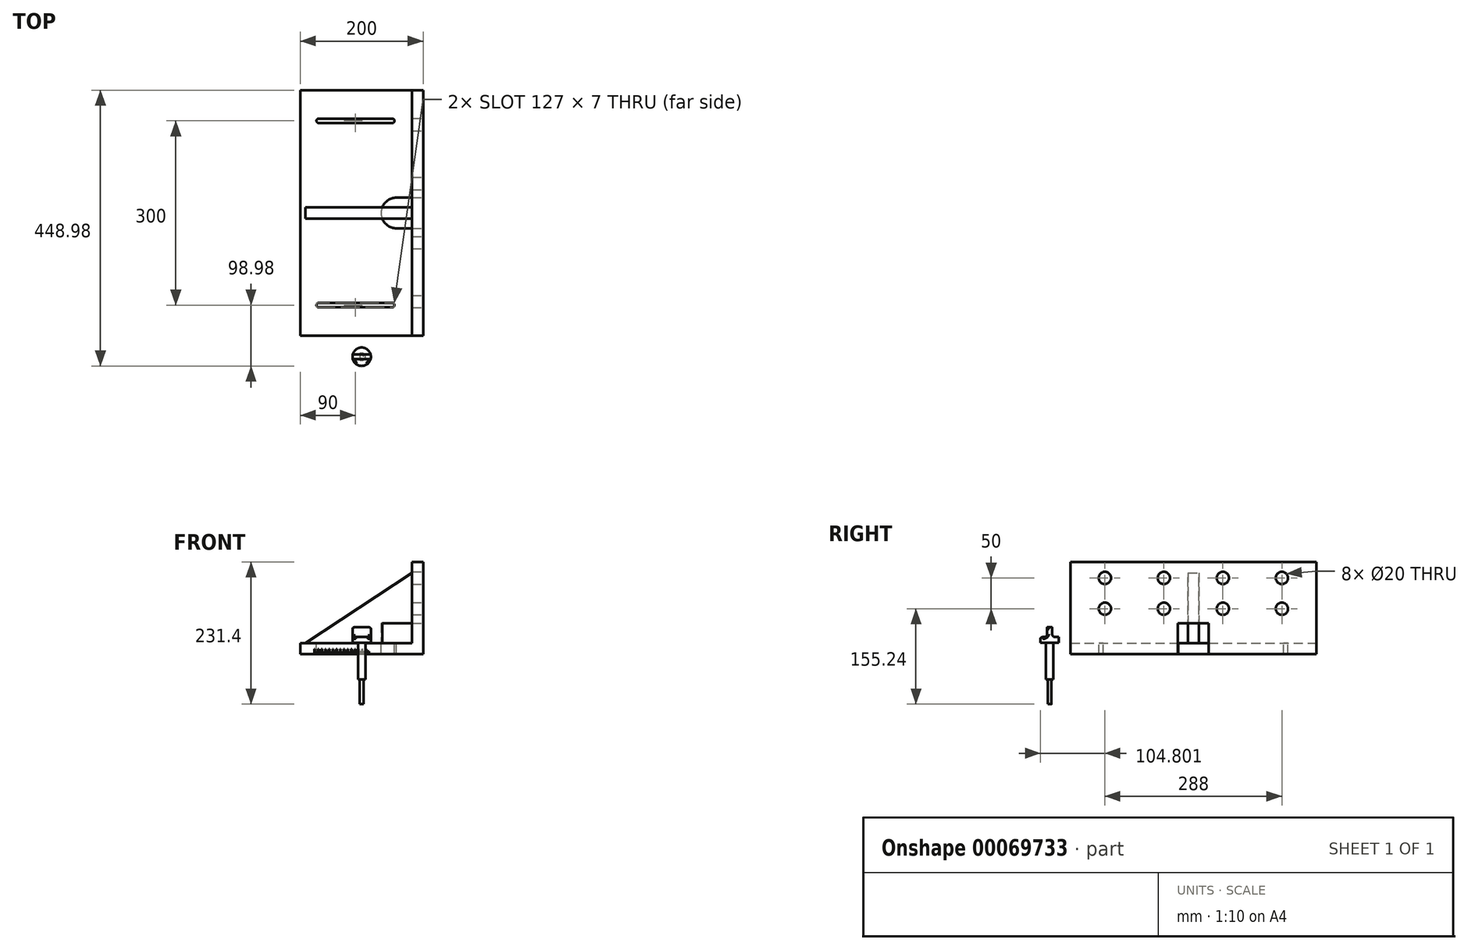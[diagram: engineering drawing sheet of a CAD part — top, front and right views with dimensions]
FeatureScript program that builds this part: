
annotation { "Feature Type Name" : "Feature", "Feature Type Description" : "" }
export const myFeature = defineFeature(function(context is Context, id is Id, definition is map)
    precondition{}
    {
        {
            var Q0;
            Q0=qCreatedBy(makeId("Front.planeOp"),FACE);
            var sketch = newSketch(context, id + "F0", { "sketchPlane" : qUnion([Q0])});
            skLineSegment(sketch, "E0.bottom", {"start": v(-100, -37.42) * mm, "end": v(82, -37.42) * mm});
            skLineSegment(sketch, "E0.top", {"start": v(-100, -55.42) * mm, "end": v(100, -55.42) * mm});
            skLineSegment(sketch, "E0.left", {"start": v(-100, -37.42) * mm, "end": v(-100, -55.42) * mm});
            skLineSegment(sketch, "E0.right", {"start": v(100, -37.42) * mm, "end": v(100, -55.42) * mm});
            skLineSegment(sketch, "E1", {"start": v(100, -37.42) * mm, "end": v(100, 94.58) * mm});
            skLineSegment(sketch, "E2", {"start": v(100, 94.58) * mm, "end": v(82, 94.58) * mm});
            skLineSegment(sketch, "E3", {"start": v(82, 94.58) * mm, "end": v(82, -37.42) * mm});
            skLineSegment(sketch, "E4", {"start": v(-91.58, -37.42) * mm, "end": v(82, 76.61) * mm});
            skSolve(sketch);
        }
        {
            var Q0;
            Q0=makeQuery(id+"F0.imprint","IMPRINT",FACE,{"disambiguationData":[TD([[makeQuery(id+"F0.imprint","IMPRINT",EDGE,{"derivedFrom":sQuery(id+"F0.wireOp",EDGE,"E0.bottom")}),-1.0]])]});
            extrude(context, id + "F1", {"entities" : qUnion([Q0]), "endBound" : BoundingType.SYMMETRIC, "depth" : 400 * mm});
        }
        {
            var Q0;
            Q0=makeQuery(id+"F1.opExtrude","SWEPT_FACE",FACE,{"disambiguationData":[OSD([sQuery(id+"F0.wireOp",EDGE,"E0.bottom")])]});
            var sketch = newSketch(context, id + "F2", { "sketchPlane" : qUnion([Q0])});
            skArc(sketch, "E5", {"start": v(-70, 153.5) * mm, "mid": v(-73.5, 150) * mm, "end": v(-70, 146.5) * mm});
            skArc(sketch, "E6", {"start": v(50, 146.5) * mm, "mid": v(53.5, 150) * mm, "end": v(50, 153.5) * mm});
            skLineSegment(sketch, "E7", {"start": v(-70, 153.5) * mm, "end": v(50, 153.5) * mm});
            skLineSegment(sketch, "E8", {"start": v(-70, 146.5) * mm, "end": v(50, 146.5) * mm});
            skLineSegment(sketch, "E9", {"start": v(-70, -153.5) * mm, "end": v(50, -153.5) * mm});
            skLineSegment(sketch, "E10", {"start": v(-70, -146.5) * mm, "end": v(50, -146.5) * mm});
            skArc(sketch, "E11", {"start": v(50, -153.5) * mm, "mid": v(53.5, -150) * mm, "end": v(50, -146.5) * mm});
            skArc(sketch, "E12", {"start": v(-70, -146.5) * mm, "mid": v(-73.5, -150) * mm, "end": v(-70, -153.5) * mm});
            skArc(sketch, "E13", {"start": v(56.66, 25) * mm, "mid": v(31.66, 0) * mm, "end": v(56.66, -25) * mm});
            skLineSegment(sketch, "E14.bottom", {"start": v(56.66, 25) * mm, "end": v(82, 25) * mm});
            skLineSegment(sketch, "E14.top", {"start": v(56.66, -25.18) * mm, "end": v(82, -25.18) * mm});
            skLineSegment(sketch, "E14.right", {"start": v(82, 25) * mm, "end": v(82, -25.18) * mm});
            skLineSegment(sketch, "E15.trimOffspring", {"start": v(56.66, -25) * mm, "end": v(56.66, -25.18) * mm});
            skSolve(sketch);
        }
        {
            var Q0;
            Q0=makeQuery(id+"F2.imprint","IMPRINT",FACE,{"disambiguationData":[TD([[makeQuery(id+"F2.imprint","IMPRINT",EDGE,{"derivedFrom":sQuery(id+"F2.wireOp",EDGE,"E5")}),1.0]])]});
            var Q1;
            Q1=makeQuery(id+"F2.imprint","IMPRINT",FACE,{"disambiguationData":[TD([[makeQuery(id+"F2.imprint","IMPRINT",EDGE,{"derivedFrom":sQuery(id+"F2.wireOp",EDGE,"E9")}),1.0]])]});
            var Q2;
            Q2=makeQuery(id+"F2.imprint","IMPRINT",FACE,{"disambiguationData":[TD([[makeQuery(id+"F2.imprint","IMPRINT",EDGE,{"derivedFrom":sQuery(id+"F2.wireOp",EDGE,"E13")}),1.0]])]});
            extrude(context, id + "F3", {"entities" : qUnion([Q0, Q1, Q2]), "operationType" : NewBodyOperationType.REMOVE, "oppositeDirection" : true, "depth" : 22 * mm});
        }
        {
            var Q0;
            Q0=makeQuery(id+"F1.opExtrude","SWEPT_FACE",FACE,{"disambiguationData":[OSD([sQuery(id+"F0.wireOp",EDGE,"E0.right"),sQuery(id+"F0.wireOp",EDGE,"E1")])]});
            var sketch = newSketch(context, id + "F4", { "sketchPlane" : qUnion([Q0])});
            skLineSegment(sketch, "E16.0", {"start": v(-25.18, -55.42) * mm, "end": v(-25.18, -37.42) * mm});
            skLineSegment(sketch, "E16.1", {"start": v(25, -55.42) * mm, "end": v(25, -37.42) * mm});
            skLineSegment(sketch, "E17.bottom", {"start": v(-25.18, -55.42) * mm, "end": v(25, -55.42) * mm});
            skLineSegment(sketch, "E17.top", {"start": v(-25.18, -5.42) * mm, "end": v(25, -5.42) * mm});
            skLineSegment(sketch, "E17.left", {"start": v(-25.18, -55.42) * mm, "end": v(-25.18, -5.42) * mm});
            skLineSegment(sketch, "E17.right", {"start": v(25, -55.42) * mm, "end": v(25, -5.42) * mm});
            skCircle(sketch, "E18", {"center": v(-144.18, 68.42) * mm, "radius": 10 * mm});
            skCircle(sketch, "E19.0.1.0", {"center": v(-144.18, 18.42) * mm, "radius": 10 * mm});
            skCircle(sketch, "E19.1.0.0", {"center": v(-48.18, 68.42) * mm, "radius": 10 * mm});
            skCircle(sketch, "E19.1.1.0", {"center": v(-48.18, 18.42) * mm, "radius": 10 * mm});
            skCircle(sketch, "E19.2.0.0", {"center": v(47.82, 68.42) * mm, "radius": 10 * mm});
            skCircle(sketch, "E19.2.1.0", {"center": v(47.82, 18.42) * mm, "radius": 10 * mm});
            skCircle(sketch, "E19.3.0.0", {"center": v(143.82, 68.42) * mm, "radius": 10 * mm});
            skCircle(sketch, "E19.3.1.0", {"center": v(143.82, 18.42) * mm, "radius": 10 * mm});
            skLineSegment(sketch, "E19.direction1", {"start": v(-144.18, 68.42) * mm, "end": v(-48.18, 68.42) * mm, "construction": true});
            skLineSegment(sketch, "E19.direction2", {"start": v(-144.18, 68.42) * mm, "end": v(-144.18, 18.42) * mm, "construction": true});
            skSolve(sketch);
        }
        {
            var Q0;
            Q0=makeQuery(id+"F4.imprint","IMPRINT",FACE,{"disambiguationData":[TD([[makeQuery(id+"F4.imprint","IMPRINT",EDGE,{"derivedFrom":sQuery(id+"F4.wireOp",EDGE,"E18")}),1.0]])]});
            var Q1;
            Q1=makeQuery(id+"F4.imprint","IMPRINT",FACE,{"disambiguationData":[TD([[makeQuery(id+"F4.imprint","IMPRINT",EDGE,{"derivedFrom":sQuery(id+"F4.wireOp",EDGE,"E19.0.1.0")}),1.0]])]});
            var Q2;
            Q2=makeQuery(id+"F4.imprint","IMPRINT",FACE,{"disambiguationData":[TD([[makeQuery(id+"F4.imprint","IMPRINT",EDGE,{"derivedFrom":sQuery(id+"F4.wireOp",EDGE,"E19.1.1.0")}),1.0]])]});
            var Q3;
            Q3=makeQuery(id+"F4.imprint","IMPRINT",FACE,{"disambiguationData":[TD([[makeQuery(id+"F4.imprint","IMPRINT",EDGE,{"derivedFrom":sQuery(id+"F4.wireOp",EDGE,"E19.1.0.0")}),1.0]])]});
            var Q4;
            Q4=makeQuery(id+"F4.imprint","IMPRINT",FACE,{"disambiguationData":[TD([[makeQuery(id+"F4.imprint","IMPRINT",EDGE,{"derivedFrom":sQuery(id+"F4.wireOp",EDGE,"E19.2.0.0")}),1.0]])]});
            var Q5;
            Q5=makeQuery(id+"F4.imprint","IMPRINT",FACE,{"disambiguationData":[TD([[makeQuery(id+"F4.imprint","IMPRINT",EDGE,{"derivedFrom":sQuery(id+"F4.wireOp",EDGE,"E19.2.1.0")}),1.0]])]});
            var Q6;
            Q6=makeQuery(id+"F4.imprint","IMPRINT",FACE,{"disambiguationData":[TD([[makeQuery(id+"F4.imprint","IMPRINT",EDGE,{"derivedFrom":sQuery(id+"F4.wireOp",EDGE,"E19.3.1.0")}),1.0]])]});
            var Q7;
            Q7=makeQuery(id+"F4.imprint","IMPRINT",FACE,{"disambiguationData":[TD([[makeQuery(id+"F4.imprint","IMPRINT",EDGE,{"derivedFrom":sQuery(id+"F4.wireOp",EDGE,"E19.3.0.0")}),1.0]])]});
            var Q8;
            {var subQ7=sQuery(id+"F4.wireOp",EDGE,"E17.top");Q8=makeQuery(id+"F4.imprint","IMPRINT",FACE,{"disambiguationData":[TD([[makeQuery(id+"F4.imprint","IMPRINT",EDGE,{"derivedFrom":subQ7}),-1.0]])]});}
            extrude(context, id + "F5", {"entities" : qUnion([Q0, Q1, Q2, Q3, Q4, Q5, Q6, Q7, Q8]), "operationType" : NewBodyOperationType.REMOVE, "oppositeDirection" : true, "depth" : 25 * mm});
        }
        {
            var Q0;
            {var subQ3=sQuery(id+"F0.wireOp",EDGE,"E4");Q0=makeQuery(id+"F0.imprint","IMPRINT",FACE,{"disambiguationData":[TD([[makeQuery(id+"F0.imprint","IMPRINT",EDGE,{"derivedFrom":subQ3}),-1.0]])]});}
            extrude(context, id + "F6", {"entities" : qUnion([Q0]), "endBound" : BoundingType.SYMMETRIC, "depth" : 18 * mm});
        }
        {
            var Q0;
            Q0=makeQuery(id+"F2.imprint","IMPRINT",FACE,{"disambiguationData":[TD([[makeQuery(id+"F2.imprint","IMPRINT",EDGE,{"derivedFrom":sQuery(id+"F2.wireOp",EDGE,"E13")}),1.0]])]});
            extrude(context, id + "F7", {"entities" : qUnion([Q0]), "operationType" : NewBodyOperationType.REMOVE, "depth" : 32 * mm});
        }
        {
            var Q0;
            Q0=qCreatedBy(makeId("Right.planeOp"),FACE);
            var sketch = newSketch(context, id + "F8", { "sketchPlane" : qUnion([Q0])});
            skLineSegment(sketch, "E20", {"start": v(-233.98, 65.01) * mm, "end": v(-233.98, -136.22) * mm, "construction": true});
            skLineSegment(sketch, "E21", {"start": v(-233.98, -136.82) * mm, "end": v(-236.98, -136.82) * mm});
            skLineSegment(sketch, "E22", {"start": v(-236.98, -136.82) * mm, "end": v(-236.98, -96.82) * mm});
            skLineSegment(sketch, "E23", {"start": v(-236.98, -96.82) * mm, "end": v(-239.98, -96.82) * mm});
            skLineSegment(sketch, "E24", {"start": v(-239.98, -96.82) * mm, "end": v(-239.98, -36.82) * mm});
            skLineSegment(sketch, "E25", {"start": v(-239.98, -36.82) * mm, "end": v(-248.98, -36.82) * mm});
            skLineSegment(sketch, "E26", {"start": v(-248.98, -36.82) * mm, "end": v(-248.98, -11.82) * mm});
            skLineSegment(sketch, "E27", {"start": v(-248.98, -11.82) * mm, "end": v(-233.98, -11.82) * mm});
            skLineSegment(sketch, "E28", {"start": v(-233.98, -136.82) * mm, "end": v(-233.98, -11.82) * mm});
            skSolve(sketch);
        }
        {
            var Q0;
            Q0=makeQuery(id+"F8.imprint","IMPRINT",FACE,{"disambiguationData":[TD([[makeQuery(id+"F8.imprint","IMPRINT",EDGE,{"derivedFrom":sQuery(id+"F8.wireOp",EDGE,"E21")}),-1.0]])]});
            var Q1;
            Q1=sQuery(id+"F8.wireOp",EDGE,"E20");
            revolve(context, id + "F9", {"entities" : qUnion([Q0]), "axis" : qUnion([Q1]), "revolveType" : RevolveType.FULL});
        }
        {
            var Q0;
            Q0=makeQuery(id+"F9.opRevolve","SWEPT_FACE",FACE,{"disambiguationData":[OSD([sQuery(id+"F8.wireOp",EDGE,"E27")])]});
            var sketch = newSketch(context, id + "F10", { "sketchPlane" : qUnion([Q0])});
            skLineSegment(sketch, "E29.bottom", {"start": v(17.05, -237.98) * mm, "end": v(-19.1, -237.98) * mm});
            skLineSegment(sketch, "E29.top", {"start": v(17.05, -250.11) * mm, "end": v(-19.1, -250.11) * mm});
            skLineSegment(sketch, "E29.left", {"start": v(17.05, -237.98) * mm, "end": v(17.05, -250.11) * mm});
            skLineSegment(sketch, "E29.right", {"start": v(-19.1, -237.98) * mm, "end": v(-19.1, -250.11) * mm});
            skLineSegment(sketch, "E30.bottom", {"start": v(17.68, -229.98) * mm, "end": v(-19.15, -229.98) * mm});
            skLineSegment(sketch, "E30.top", {"start": v(17.68, -217.98) * mm, "end": v(-19.15, -217.98) * mm});
            skLineSegment(sketch, "E30.left", {"start": v(17.68, -229.98) * mm, "end": v(17.68, -217.98) * mm});
            skLineSegment(sketch, "E30.right", {"start": v(-19.15, -229.98) * mm, "end": v(-19.15, -217.98) * mm});
            skSolve(sketch);
        }
        {
            var Q0;
            {var subQ0=sQuery(id+"F10.wireOp",EDGE,"E29.bottom");var subQ1=makeQuery(id+"F9.opRevolve","SWEPT_EDGE",EDGE,{"disambiguationData":[OSD([sQuery(id+"F8.wireOp",EDGE,"E26"),sQuery(id+"F8.wireOp",EDGE,"E27")])]});var subQ2=makeQuery(id+"F10.imprint","INTERSECT",VERTEX,{"disambiguationData":[OD(0.0)],"derivedFrom":[subQ1,subQ0]});Q0=makeQuery(id+"F10.imprint","IMPRINT",FACE,{"disambiguationData":[TD([[makeQuery(id+"F10.imprint","IMPRINT",EDGE,{"disambiguationData":[TD([[subQ2,-1.0]])],"derivedFrom":subQ0}),1.0]])]});}
            var Q1;
            Q1=makeQuery(id+"F10.imprint","IMPRINT",FACE,{"disambiguationData":[TD([[makeQuery(id+"F10.imprint","IMPRINT",EDGE,{"derivedFrom":sQuery(id+"F10.wireOp",EDGE,"E29.top")}),-1.0]])]});
            var Q2;
            {var subQ0=sQuery(id+"F10.wireOp",EDGE,"E30.bottom");var subQ1=makeQuery(id+"F9.opRevolve","SWEPT_EDGE",EDGE,{"disambiguationData":[OSD([sQuery(id+"F8.wireOp",EDGE,"E26"),sQuery(id+"F8.wireOp",EDGE,"E27")])]});var subQ2=makeQuery(id+"F10.imprint","INTERSECT",VERTEX,{"disambiguationData":[OD(0.0)],"derivedFrom":[subQ1,subQ0]});Q2=makeQuery(id+"F10.imprint","IMPRINT",FACE,{"disambiguationData":[TD([[makeQuery(id+"F10.imprint","IMPRINT",EDGE,{"disambiguationData":[TD([[subQ2,-1.0]])],"derivedFrom":subQ0}),-1.0]])]});}
            extrude(context, id + "F11", {"entities" : qUnion([Q0, Q1, Q2]), "operationType" : NewBodyOperationType.REMOVE, "oppositeDirection" : true, "depth" : 16 * mm});
        }
        {
            var Q0;
            Q0=makeQuery(id+"F11.boolean.opBoolean","COPY",EDGE,{"derivedFrom":makeQuery(id+"F11.opExtrude","CAP_EDGE",EDGE,{"disambiguationData":[OSD([sQuery(id+"F10.wireOp",EDGE,"E29.bottom")])],"isStart":false})});
            var Q1;
            Q1=makeQuery(id+"F11.boolean.opBoolean","COPY",EDGE,{"derivedFrom":makeQuery(id+"F11.opExtrude","CAP_EDGE",EDGE,{"disambiguationData":[OSD([sQuery(id+"F10.wireOp",EDGE,"E30.bottom")])],"isStart":false})});
            fillet(context, id + "F12", {"entities" : qUnion([Q0, Q1]), "radius" : 5 * mm, "tangentPropagation" : true, "allowEdgeOverflow" : false});
        }
        {
            var Q0;
            Q0=makeQuery(id+"F11.boolean.opBoolean","INTERSECT",EDGE,{"disambiguationData":[OD(0.0)],"derivedFrom":[makeQuery(id+"F9.opRevolve","SWEPT_FACE",FACE,{"disambiguationData":[OSD([sQuery(id+"F8.wireOp",EDGE,"E26")])]}),makeQuery(id+"F11.opExtrude","SWEPT_FACE",FACE,{"disambiguationData":[OSD([sQuery(id+"F10.wireOp",EDGE,"E29.bottom")])]})]});
            var Q1;
            {var subQ0=sQuery(id+"F10.wireOp",EDGE,"E30.bottom");var subQ1=sQuery(id+"F8.wireOp",EDGE,"E27");var subQ2=sQuery(id+"F8.wireOp",EDGE,"E26");Q1=makeQuery(id+"F11.boolean.opBoolean","COPY",EDGE,{"derivedFrom":makeQuery(id+"F11.opExtrude","SWEPT_EDGE",EDGE,{"disambiguationData":[OSD([subQ2,subQ1,subQ0]),TDD([makeQuery(id+"F10.imprint","INTERSECT",VERTEX,{"disambiguationData":[OD(0.0)],"derivedFrom":[makeQuery(id+"F9.opRevolve","SWEPT_EDGE",EDGE,{"disambiguationData":[OSD([subQ2,subQ1])]}),subQ0]})])]})});}
            var Q2;
            Q2=makeQuery(id+"F11.boolean.opBoolean","SPLIT",EDGE,{"disambiguationData":[OD(0.0)],"derivedFrom":makeQuery(id+"F9.opRevolve","SWEPT_EDGE",EDGE,{"disambiguationData":[OSD([sQuery(id+"F8.wireOp",EDGE,"E26"),sQuery(id+"F8.wireOp",EDGE,"E27")])]})});
            var Q3;
            Q3=makeQuery(id+"F11.boolean.opBoolean","COPY",EDGE,{"derivedFrom":makeQuery(id+"F11.opExtrude","CAP_EDGE",EDGE,{"disambiguationData":[OSD([sQuery(id+"F10.wireOp",EDGE,"E29.bottom")])],"isStart":true})});
            var Q4;
            Q4=makeQuery(id+"F11.boolean.opBoolean","COPY",EDGE,{"derivedFrom":makeQuery(id+"F11.opExtrude","CAP_EDGE",EDGE,{"disambiguationData":[OSD([sQuery(id+"F10.wireOp",EDGE,"E30.bottom")])],"isStart":true})});
            var Q5;
            Q5=makeQuery(id+"F11.boolean.opBoolean","INTERSECT",EDGE,{"disambiguationData":[OD(1.0)],"derivedFrom":[makeQuery(id+"F9.opRevolve","SWEPT_FACE",FACE,{"disambiguationData":[OSD([sQuery(id+"F8.wireOp",EDGE,"E26")])]}),makeQuery(id+"F11.opExtrude","SWEPT_FACE",FACE,{"disambiguationData":[OSD([sQuery(id+"F10.wireOp",EDGE,"E29.bottom")])]})]});
            var Q6;
            {var subQ0=sQuery(id+"F10.wireOp",EDGE,"E30.bottom");var subQ1=sQuery(id+"F8.wireOp",EDGE,"E27");var subQ2=sQuery(id+"F8.wireOp",EDGE,"E26");Q6=makeQuery(id+"F11.boolean.opBoolean","COPY",EDGE,{"derivedFrom":makeQuery(id+"F11.opExtrude","SWEPT_EDGE",EDGE,{"disambiguationData":[OSD([subQ2,subQ1,subQ0]),TDD([makeQuery(id+"F10.imprint","INTERSECT",VERTEX,{"disambiguationData":[OD(1.0)],"derivedFrom":[makeQuery(id+"F9.opRevolve","SWEPT_EDGE",EDGE,{"disambiguationData":[OSD([subQ2,subQ1])]}),subQ0]})])]})});}
            var Q7;
            Q7=makeQuery(id+"F11.boolean.opBoolean","SPLIT",EDGE,{"disambiguationData":[OD(1.0)],"derivedFrom":makeQuery(id+"F9.opRevolve","SWEPT_EDGE",EDGE,{"disambiguationData":[OSD([sQuery(id+"F8.wireOp",EDGE,"E26"),sQuery(id+"F8.wireOp",EDGE,"E27")])]})});
            fillet(context, id + "F13", {"entities" : qUnion([Q0, Q1, Q2, Q3, Q4, Q5, Q6, Q7]), "radius" : 3 * mm, "tangentPropagation" : true, "allowEdgeOverflow" : false});
        }
        {
            var Q0;
            Q0=makeQuery(id+"F1.opExtrude","CAP_FACE",FACE,{"disambiguationData":[OSD([sQuery(id+"F0.wireOp",EDGE,"E0.bottom"),sQuery(id+"F0.wireOp",EDGE,"E0.top"),sQuery(id+"F0.wireOp",EDGE,"E0.left"),sQuery(id+"F0.wireOp",EDGE,"E0.right"),sQuery(id+"F0.wireOp",EDGE,"E1"),sQuery(id+"F0.wireOp",EDGE,"E2"),sQuery(id+"F0.wireOp",EDGE,"E3")])],"isStart":false});
            var sketch = newSketch(context, id + "F14", { "sketchPlane" : qUnion([Q0])});
            skLineSegment(sketch, "E31.bottom", {"start": v(-77.2, -55.42) * mm, "end": v(-76.2, -55.42) * mm});
            skLineSegment(sketch, "E31.top", {"start": v(-77.2, -47.42) * mm, "end": v(-76.2, -47.42) * mm});
            skLineSegment(sketch, "E31.left", {"start": v(-77.2, -55.42) * mm, "end": v(-77.2, -47.42) * mm});
            skLineSegment(sketch, "E31.right", {"start": v(-76.2, -55.42) * mm, "end": v(-76.2, -47.42) * mm});
            skLineSegment(sketch, "E32.bottom", {"start": v(-75.2, -55.42) * mm, "end": v(-74.2, -55.42) * mm});
            skLineSegment(sketch, "E32.top", {"start": v(-75.2, -50.86) * mm, "end": v(-74.2, -50.86) * mm});
            skLineSegment(sketch, "E32.left", {"start": v(-75.2, -55.42) * mm, "end": v(-75.2, -50.86) * mm});
            skLineSegment(sketch, "E32.right", {"start": v(-74.2, -55.42) * mm, "end": v(-74.2, -50.86) * mm});
            skLineSegment(sketch, "E33.bottom", {"start": v(-73.2, -55.42) * mm, "end": v(-72.2, -55.42) * mm});
            skLineSegment(sketch, "E33.top", {"start": v(-73.2, -50.86) * mm, "end": v(-72.2, -50.86) * mm});
            skLineSegment(sketch, "E33.left", {"start": v(-73.2, -55.42) * mm, "end": v(-73.2, -50.86) * mm});
            skLineSegment(sketch, "E33.right", {"start": v(-72.2, -55.42) * mm, "end": v(-72.2, -50.86) * mm});
            skLineSegment(sketch, "E34.1.0.0", {"start": v(-69.2, -55.42) * mm, "end": v(-69.2, -50.86) * mm});
            skLineSegment(sketch, "E34.1.0.1", {"start": v(-70.2, -55.42) * mm, "end": v(-70.2, -47.42) * mm});
            skLineSegment(sketch, "E34.1.0.2", {"start": v(-71.2, -55.42) * mm, "end": v(-71.2, -47.42) * mm});
            skLineSegment(sketch, "E34.1.0.3", {"start": v(-68.2, -55.42) * mm, "end": v(-68.2, -50.86) * mm});
            skLineSegment(sketch, "E34.1.0.4", {"start": v(-67.2, -55.42) * mm, "end": v(-66.2, -55.42) * mm});
            skLineSegment(sketch, "E34.1.0.5", {"start": v(-67.2, -50.86) * mm, "end": v(-66.2, -50.86) * mm});
            skLineSegment(sketch, "E34.1.0.6", {"start": v(-67.2, -55.42) * mm, "end": v(-67.2, -50.86) * mm});
            skLineSegment(sketch, "E34.1.0.7", {"start": v(-66.2, -55.42) * mm, "end": v(-66.2, -50.86) * mm});
            skLineSegment(sketch, "E34.1.0.8", {"start": v(-69.2, -50.86) * mm, "end": v(-68.2, -50.86) * mm});
            skLineSegment(sketch, "E34.1.0.9", {"start": v(-69.2, -55.42) * mm, "end": v(-68.2, -55.42) * mm});
            skLineSegment(sketch, "E34.1.0.10", {"start": v(-71.2, -47.42) * mm, "end": v(-70.2, -47.42) * mm});
            skLineSegment(sketch, "E34.1.0.11", {"start": v(-71.2, -55.42) * mm, "end": v(-70.2, -55.42) * mm});
            skLineSegment(sketch, "E34.2.0.0", {"start": v(-63.2, -55.42) * mm, "end": v(-63.2, -50.86) * mm});
            skLineSegment(sketch, "E34.2.0.1", {"start": v(-64.2, -55.42) * mm, "end": v(-64.2, -47.42) * mm});
            skLineSegment(sketch, "E34.2.0.2", {"start": v(-65.2, -55.42) * mm, "end": v(-65.2, -47.42) * mm});
            skLineSegment(sketch, "E34.2.0.3", {"start": v(-62.2, -55.42) * mm, "end": v(-62.2, -50.86) * mm});
            skLineSegment(sketch, "E34.2.0.4", {"start": v(-61.2, -55.42) * mm, "end": v(-60.2, -55.42) * mm});
            skLineSegment(sketch, "E34.2.0.5", {"start": v(-61.2, -50.86) * mm, "end": v(-60.2, -50.86) * mm});
            skLineSegment(sketch, "E34.2.0.6", {"start": v(-61.2, -55.42) * mm, "end": v(-61.2, -50.86) * mm});
            skLineSegment(sketch, "E34.2.0.7", {"start": v(-60.2, -55.42) * mm, "end": v(-60.2, -50.86) * mm});
            skLineSegment(sketch, "E34.2.0.8", {"start": v(-63.2, -50.86) * mm, "end": v(-62.2, -50.86) * mm});
            skLineSegment(sketch, "E34.2.0.9", {"start": v(-63.2, -55.42) * mm, "end": v(-62.2, -55.42) * mm});
            skLineSegment(sketch, "E34.2.0.10", {"start": v(-65.2, -47.42) * mm, "end": v(-64.2, -47.42) * mm});
            skLineSegment(sketch, "E34.2.0.11", {"start": v(-65.2, -55.42) * mm, "end": v(-64.2, -55.42) * mm});
            skLineSegment(sketch, "E34.3.0.0", {"start": v(-57.2, -55.42) * mm, "end": v(-57.2, -50.86) * mm});
            skLineSegment(sketch, "E34.3.0.1", {"start": v(-58.2, -55.42) * mm, "end": v(-58.2, -47.42) * mm});
            skLineSegment(sketch, "E34.3.0.2", {"start": v(-59.2, -55.42) * mm, "end": v(-59.2, -47.42) * mm});
            skLineSegment(sketch, "E34.3.0.3", {"start": v(-56.2, -55.42) * mm, "end": v(-56.2, -50.86) * mm});
            skLineSegment(sketch, "E34.3.0.4", {"start": v(-55.2, -55.42) * mm, "end": v(-54.2, -55.42) * mm});
            skLineSegment(sketch, "E34.3.0.5", {"start": v(-55.2, -50.86) * mm, "end": v(-54.2, -50.86) * mm});
            skLineSegment(sketch, "E34.3.0.6", {"start": v(-55.2, -55.42) * mm, "end": v(-55.2, -50.86) * mm});
            skLineSegment(sketch, "E34.3.0.7", {"start": v(-54.2, -55.42) * mm, "end": v(-54.2, -50.86) * mm});
            skLineSegment(sketch, "E34.3.0.8", {"start": v(-57.2, -50.86) * mm, "end": v(-56.2, -50.86) * mm});
            skLineSegment(sketch, "E34.3.0.9", {"start": v(-57.2, -55.42) * mm, "end": v(-56.2, -55.42) * mm});
            skLineSegment(sketch, "E34.3.0.10", {"start": v(-59.2, -47.42) * mm, "end": v(-58.2, -47.42) * mm});
            skLineSegment(sketch, "E34.3.0.11", {"start": v(-59.2, -55.42) * mm, "end": v(-58.2, -55.42) * mm});
            skLineSegment(sketch, "E34.4.0.0", {"start": v(-51.2, -55.42) * mm, "end": v(-51.2, -50.86) * mm});
            skLineSegment(sketch, "E34.4.0.1", {"start": v(-52.2, -55.42) * mm, "end": v(-52.2, -47.42) * mm});
            skLineSegment(sketch, "E34.4.0.2", {"start": v(-53.2, -55.42) * mm, "end": v(-53.2, -47.42) * mm});
            skLineSegment(sketch, "E34.4.0.3", {"start": v(-50.2, -55.42) * mm, "end": v(-50.2, -50.86) * mm});
            skLineSegment(sketch, "E34.4.0.4", {"start": v(-49.2, -55.42) * mm, "end": v(-48.2, -55.42) * mm});
            skLineSegment(sketch, "E34.4.0.5", {"start": v(-49.2, -50.86) * mm, "end": v(-48.2, -50.86) * mm});
            skLineSegment(sketch, "E34.4.0.6", {"start": v(-49.2, -55.42) * mm, "end": v(-49.2, -50.86) * mm});
            skLineSegment(sketch, "E34.4.0.7", {"start": v(-48.2, -55.42) * mm, "end": v(-48.2, -50.86) * mm});
            skLineSegment(sketch, "E34.4.0.8", {"start": v(-51.2, -50.86) * mm, "end": v(-50.2, -50.86) * mm});
            skLineSegment(sketch, "E34.4.0.9", {"start": v(-51.2, -55.42) * mm, "end": v(-50.2, -55.42) * mm});
            skLineSegment(sketch, "E34.4.0.10", {"start": v(-53.2, -47.42) * mm, "end": v(-52.2, -47.42) * mm});
            skLineSegment(sketch, "E34.4.0.11", {"start": v(-53.2, -55.42) * mm, "end": v(-52.2, -55.42) * mm});
            skLineSegment(sketch, "E34.5.0.0", {"start": v(-45.2, -55.42) * mm, "end": v(-45.2, -50.86) * mm});
            skLineSegment(sketch, "E34.5.0.1", {"start": v(-46.2, -55.42) * mm, "end": v(-46.2, -47.42) * mm});
            skLineSegment(sketch, "E34.5.0.2", {"start": v(-47.2, -55.42) * mm, "end": v(-47.2, -47.42) * mm});
            skLineSegment(sketch, "E34.5.0.3", {"start": v(-44.2, -55.42) * mm, "end": v(-44.2, -50.86) * mm});
            skLineSegment(sketch, "E34.5.0.4", {"start": v(-43.2, -55.42) * mm, "end": v(-42.2, -55.42) * mm});
            skLineSegment(sketch, "E34.5.0.5", {"start": v(-43.2, -50.86) * mm, "end": v(-42.2, -50.86) * mm});
            skLineSegment(sketch, "E34.5.0.6", {"start": v(-43.2, -55.42) * mm, "end": v(-43.2, -50.86) * mm});
            skLineSegment(sketch, "E34.5.0.7", {"start": v(-42.2, -55.42) * mm, "end": v(-42.2, -50.86) * mm});
            skLineSegment(sketch, "E34.5.0.8", {"start": v(-45.2, -50.86) * mm, "end": v(-44.2, -50.86) * mm});
            skLineSegment(sketch, "E34.5.0.9", {"start": v(-45.2, -55.42) * mm, "end": v(-44.2, -55.42) * mm});
            skLineSegment(sketch, "E34.5.0.10", {"start": v(-47.2, -47.42) * mm, "end": v(-46.2, -47.42) * mm});
            skLineSegment(sketch, "E34.5.0.11", {"start": v(-47.2, -55.42) * mm, "end": v(-46.2, -55.42) * mm});
            skLineSegment(sketch, "E34.6.0.0", {"start": v(-39.2, -55.42) * mm, "end": v(-39.2, -50.86) * mm});
            skLineSegment(sketch, "E34.6.0.1", {"start": v(-40.2, -55.42) * mm, "end": v(-40.2, -47.42) * mm});
            skLineSegment(sketch, "E34.6.0.2", {"start": v(-41.2, -55.42) * mm, "end": v(-41.2, -47.42) * mm});
            skLineSegment(sketch, "E34.6.0.3", {"start": v(-38.2, -55.42) * mm, "end": v(-38.2, -50.86) * mm});
            skLineSegment(sketch, "E34.6.0.4", {"start": v(-37.2, -55.42) * mm, "end": v(-36.2, -55.42) * mm});
            skLineSegment(sketch, "E34.6.0.5", {"start": v(-37.2, -50.86) * mm, "end": v(-36.2, -50.86) * mm});
            skLineSegment(sketch, "E34.6.0.6", {"start": v(-37.2, -55.42) * mm, "end": v(-37.2, -50.86) * mm});
            skLineSegment(sketch, "E34.6.0.7", {"start": v(-36.2, -55.42) * mm, "end": v(-36.2, -50.86) * mm});
            skLineSegment(sketch, "E34.6.0.8", {"start": v(-39.2, -50.86) * mm, "end": v(-38.2, -50.86) * mm});
            skLineSegment(sketch, "E34.6.0.9", {"start": v(-39.2, -55.42) * mm, "end": v(-38.2, -55.42) * mm});
            skLineSegment(sketch, "E34.6.0.10", {"start": v(-41.2, -47.42) * mm, "end": v(-40.2, -47.42) * mm});
            skLineSegment(sketch, "E34.6.0.11", {"start": v(-41.2, -55.42) * mm, "end": v(-40.2, -55.42) * mm});
            skLineSegment(sketch, "E34.7.0.0", {"start": v(-33.2, -55.42) * mm, "end": v(-33.2, -50.86) * mm});
            skLineSegment(sketch, "E34.7.0.1", {"start": v(-34.2, -55.42) * mm, "end": v(-34.2, -47.42) * mm});
            skLineSegment(sketch, "E34.7.0.2", {"start": v(-35.2, -55.42) * mm, "end": v(-35.2, -47.42) * mm});
            skLineSegment(sketch, "E34.7.0.3", {"start": v(-32.2, -55.42) * mm, "end": v(-32.2, -50.86) * mm});
            skLineSegment(sketch, "E34.7.0.4", {"start": v(-31.2, -55.42) * mm, "end": v(-30.2, -55.42) * mm});
            skLineSegment(sketch, "E34.7.0.5", {"start": v(-31.2, -50.86) * mm, "end": v(-30.2, -50.86) * mm});
            skLineSegment(sketch, "E34.7.0.6", {"start": v(-31.2, -55.42) * mm, "end": v(-31.2, -50.86) * mm});
            skLineSegment(sketch, "E34.7.0.7", {"start": v(-30.2, -55.42) * mm, "end": v(-30.2, -50.86) * mm});
            skLineSegment(sketch, "E34.7.0.8", {"start": v(-33.2, -50.86) * mm, "end": v(-32.2, -50.86) * mm});
            skLineSegment(sketch, "E34.7.0.9", {"start": v(-33.2, -55.42) * mm, "end": v(-32.2, -55.42) * mm});
            skLineSegment(sketch, "E34.7.0.10", {"start": v(-35.2, -47.42) * mm, "end": v(-34.2, -47.42) * mm});
            skLineSegment(sketch, "E34.7.0.11", {"start": v(-35.2, -55.42) * mm, "end": v(-34.2, -55.42) * mm});
            skLineSegment(sketch, "E34.8.0.0", {"start": v(-27.2, -55.42) * mm, "end": v(-27.2, -50.86) * mm});
            skLineSegment(sketch, "E34.8.0.1", {"start": v(-28.2, -55.42) * mm, "end": v(-28.2, -47.42) * mm});
            skLineSegment(sketch, "E34.8.0.2", {"start": v(-29.2, -55.42) * mm, "end": v(-29.2, -47.42) * mm});
            skLineSegment(sketch, "E34.8.0.3", {"start": v(-26.2, -55.42) * mm, "end": v(-26.2, -50.86) * mm});
            skLineSegment(sketch, "E34.8.0.4", {"start": v(-25.2, -55.42) * mm, "end": v(-24.2, -55.42) * mm});
            skLineSegment(sketch, "E34.8.0.5", {"start": v(-25.2, -50.86) * mm, "end": v(-24.2, -50.86) * mm});
            skLineSegment(sketch, "E34.8.0.6", {"start": v(-25.2, -55.42) * mm, "end": v(-25.2, -50.86) * mm});
            skLineSegment(sketch, "E34.8.0.7", {"start": v(-24.2, -55.42) * mm, "end": v(-24.2, -50.86) * mm});
            skLineSegment(sketch, "E34.8.0.8", {"start": v(-27.2, -50.86) * mm, "end": v(-26.2, -50.86) * mm});
            skLineSegment(sketch, "E34.8.0.9", {"start": v(-27.2, -55.42) * mm, "end": v(-26.2, -55.42) * mm});
            skLineSegment(sketch, "E34.8.0.10", {"start": v(-29.2, -47.42) * mm, "end": v(-28.2, -47.42) * mm});
            skLineSegment(sketch, "E34.8.0.11", {"start": v(-29.2, -55.42) * mm, "end": v(-28.2, -55.42) * mm});
            skLineSegment(sketch, "E34.9.0.0", {"start": v(-21.2, -55.42) * mm, "end": v(-21.2, -50.86) * mm});
            skLineSegment(sketch, "E34.9.0.1", {"start": v(-22.2, -55.42) * mm, "end": v(-22.2, -47.42) * mm});
            skLineSegment(sketch, "E34.9.0.2", {"start": v(-23.2, -55.42) * mm, "end": v(-23.2, -47.42) * mm});
            skLineSegment(sketch, "E34.9.0.3", {"start": v(-20.2, -55.42) * mm, "end": v(-20.2, -50.86) * mm});
            skLineSegment(sketch, "E34.9.0.4", {"start": v(-19.2, -55.42) * mm, "end": v(-18.2, -55.42) * mm});
            skLineSegment(sketch, "E34.9.0.5", {"start": v(-19.2, -50.86) * mm, "end": v(-18.2, -50.86) * mm});
            skLineSegment(sketch, "E34.9.0.6", {"start": v(-19.2, -55.42) * mm, "end": v(-19.2, -50.86) * mm});
            skLineSegment(sketch, "E34.9.0.7", {"start": v(-18.2, -55.42) * mm, "end": v(-18.2, -50.86) * mm});
            skLineSegment(sketch, "E34.9.0.8", {"start": v(-21.2, -50.86) * mm, "end": v(-20.2, -50.86) * mm});
            skLineSegment(sketch, "E34.9.0.9", {"start": v(-21.2, -55.42) * mm, "end": v(-20.2, -55.42) * mm});
            skLineSegment(sketch, "E34.9.0.10", {"start": v(-23.2, -47.42) * mm, "end": v(-22.2, -47.42) * mm});
            skLineSegment(sketch, "E34.9.0.11", {"start": v(-23.2, -55.42) * mm, "end": v(-22.2, -55.42) * mm});
            skLineSegment(sketch, "E34.10.0.0", {"start": v(-15.2, -55.42) * mm, "end": v(-15.2, -50.86) * mm});
            skLineSegment(sketch, "E34.10.0.1", {"start": v(-16.2, -55.42) * mm, "end": v(-16.2, -47.42) * mm});
            skLineSegment(sketch, "E34.10.0.2", {"start": v(-17.2, -55.42) * mm, "end": v(-17.2, -47.42) * mm});
            skLineSegment(sketch, "E34.10.0.3", {"start": v(-14.2, -55.42) * mm, "end": v(-14.2, -50.86) * mm});
            skLineSegment(sketch, "E34.10.0.4", {"start": v(-13.2, -55.42) * mm, "end": v(-12.2, -55.42) * mm});
            skLineSegment(sketch, "E34.10.0.5", {"start": v(-13.2, -50.86) * mm, "end": v(-12.2, -50.86) * mm});
            skLineSegment(sketch, "E34.10.0.6", {"start": v(-13.2, -55.42) * mm, "end": v(-13.2, -50.86) * mm});
            skLineSegment(sketch, "E34.10.0.7", {"start": v(-12.2, -55.42) * mm, "end": v(-12.2, -50.86) * mm});
            skLineSegment(sketch, "E34.10.0.8", {"start": v(-15.2, -50.86) * mm, "end": v(-14.2, -50.86) * mm});
            skLineSegment(sketch, "E34.10.0.9", {"start": v(-15.2, -55.42) * mm, "end": v(-14.2, -55.42) * mm});
            skLineSegment(sketch, "E34.10.0.10", {"start": v(-17.2, -47.42) * mm, "end": v(-16.2, -47.42) * mm});
            skLineSegment(sketch, "E34.10.0.11", {"start": v(-17.2, -55.42) * mm, "end": v(-16.2, -55.42) * mm});
            skLineSegment(sketch, "E34.11.0.0", {"start": v(-9.2, -55.42) * mm, "end": v(-9.2, -50.86) * mm});
            skLineSegment(sketch, "E34.11.0.1", {"start": v(-10.2, -55.42) * mm, "end": v(-10.2, -47.42) * mm});
            skLineSegment(sketch, "E34.11.0.2", {"start": v(-11.2, -55.42) * mm, "end": v(-11.2, -47.42) * mm});
            skLineSegment(sketch, "E34.11.0.3", {"start": v(-8.2, -55.42) * mm, "end": v(-8.2, -50.86) * mm});
            skLineSegment(sketch, "E34.11.0.4", {"start": v(-7.2, -55.42) * mm, "end": v(-6.2, -55.42) * mm});
            skLineSegment(sketch, "E34.11.0.5", {"start": v(-7.2, -50.86) * mm, "end": v(-6.2, -50.86) * mm});
            skLineSegment(sketch, "E34.11.0.6", {"start": v(-7.2, -55.42) * mm, "end": v(-7.2, -50.86) * mm});
            skLineSegment(sketch, "E34.11.0.7", {"start": v(-6.2, -55.42) * mm, "end": v(-6.2, -50.86) * mm});
            skLineSegment(sketch, "E34.11.0.8", {"start": v(-9.2, -50.86) * mm, "end": v(-8.2, -50.86) * mm});
            skLineSegment(sketch, "E34.11.0.9", {"start": v(-9.2, -55.42) * mm, "end": v(-8.2, -55.42) * mm});
            skLineSegment(sketch, "E34.11.0.10", {"start": v(-11.2, -47.42) * mm, "end": v(-10.2, -47.42) * mm});
            skLineSegment(sketch, "E34.11.0.11", {"start": v(-11.2, -55.42) * mm, "end": v(-10.2, -55.42) * mm});
            skLineSegment(sketch, "E34.12.0.0", {"start": v(-3.2, -55.42) * mm, "end": v(-3.2, -50.86) * mm});
            skLineSegment(sketch, "E34.12.0.1", {"start": v(-4.2, -55.42) * mm, "end": v(-4.2, -47.42) * mm});
            skLineSegment(sketch, "E34.12.0.2", {"start": v(-5.2, -55.42) * mm, "end": v(-5.2, -47.42) * mm});
            skLineSegment(sketch, "E34.12.0.3", {"start": v(-2.2, -55.42) * mm, "end": v(-2.2, -50.86) * mm});
            skLineSegment(sketch, "E34.12.0.4", {"start": v(-1.2, -55.42) * mm, "end": v(-0.2, -55.42) * mm});
            skLineSegment(sketch, "E34.12.0.5", {"start": v(-1.2, -50.86) * mm, "end": v(-0.2, -50.86) * mm});
            skLineSegment(sketch, "E34.12.0.6", {"start": v(-1.2, -55.42) * mm, "end": v(-1.2, -50.86) * mm});
            skLineSegment(sketch, "E34.12.0.7", {"start": v(-0.2, -55.42) * mm, "end": v(-0.2, -50.86) * mm});
            skLineSegment(sketch, "E34.12.0.8", {"start": v(-3.2, -50.86) * mm, "end": v(-2.2, -50.86) * mm});
            skLineSegment(sketch, "E34.12.0.9", {"start": v(-3.2, -55.42) * mm, "end": v(-2.2, -55.42) * mm});
            skLineSegment(sketch, "E34.12.0.10", {"start": v(-5.2, -47.42) * mm, "end": v(-4.2, -47.42) * mm});
            skLineSegment(sketch, "E34.12.0.11", {"start": v(-5.2, -55.42) * mm, "end": v(-4.2, -55.42) * mm});
            skLineSegment(sketch, "E34.13.0.0", {"start": v(2.8, -55.42) * mm, "end": v(2.8, -50.86) * mm});
            skLineSegment(sketch, "E34.13.0.1", {"start": v(1.8, -55.42) * mm, "end": v(1.8, -47.42) * mm});
            skLineSegment(sketch, "E34.13.0.2", {"start": v(0.8, -55.42) * mm, "end": v(0.8, -47.42) * mm});
            skLineSegment(sketch, "E34.13.0.3", {"start": v(3.8, -55.42) * mm, "end": v(3.8, -50.86) * mm});
            skLineSegment(sketch, "E34.13.0.4", {"start": v(4.8, -55.42) * mm, "end": v(5.8, -55.42) * mm});
            skLineSegment(sketch, "E34.13.0.5", {"start": v(4.8, -50.86) * mm, "end": v(5.8, -50.86) * mm});
            skLineSegment(sketch, "E34.13.0.6", {"start": v(4.8, -55.42) * mm, "end": v(4.8, -50.86) * mm});
            skLineSegment(sketch, "E34.13.0.7", {"start": v(5.8, -55.42) * mm, "end": v(5.8, -50.86) * mm});
            skLineSegment(sketch, "E34.13.0.8", {"start": v(2.8, -50.86) * mm, "end": v(3.8, -50.86) * mm});
            skLineSegment(sketch, "E34.13.0.9", {"start": v(2.8, -55.42) * mm, "end": v(3.8, -55.42) * mm});
            skLineSegment(sketch, "E34.13.0.10", {"start": v(0.8, -47.42) * mm, "end": v(1.8, -47.42) * mm});
            skLineSegment(sketch, "E34.13.0.11", {"start": v(0.8, -55.42) * mm, "end": v(1.8, -55.42) * mm});
            skLineSegment(sketch, "E34.14.0.0", {"start": v(8.8, -55.42) * mm, "end": v(8.8, -50.86) * mm});
            skLineSegment(sketch, "E34.14.0.1", {"start": v(7.8, -55.42) * mm, "end": v(7.8, -47.42) * mm});
            skLineSegment(sketch, "E34.14.0.2", {"start": v(6.8, -55.42) * mm, "end": v(6.8, -47.42) * mm});
            skLineSegment(sketch, "E34.14.0.3", {"start": v(9.8, -55.42) * mm, "end": v(9.8, -50.86) * mm});
            skLineSegment(sketch, "E34.14.0.4", {"start": v(10.8, -55.42) * mm, "end": v(11.8, -55.42) * mm});
            skLineSegment(sketch, "E34.14.0.5", {"start": v(10.8, -50.86) * mm, "end": v(11.8, -50.86) * mm});
            skLineSegment(sketch, "E34.14.0.6", {"start": v(10.8, -55.42) * mm, "end": v(10.8, -50.86) * mm});
            skLineSegment(sketch, "E34.14.0.7", {"start": v(11.8, -55.42) * mm, "end": v(11.8, -50.86) * mm});
            skLineSegment(sketch, "E34.14.0.8", {"start": v(8.8, -50.86) * mm, "end": v(9.8, -50.86) * mm});
            skLineSegment(sketch, "E34.14.0.9", {"start": v(8.8, -55.42) * mm, "end": v(9.8, -55.42) * mm});
            skLineSegment(sketch, "E34.14.0.10", {"start": v(6.8, -47.42) * mm, "end": v(7.8, -47.42) * mm});
            skLineSegment(sketch, "E34.14.0.11", {"start": v(6.8, -55.42) * mm, "end": v(7.8, -55.42) * mm});
            skLineSegment(sketch, "E34.direction1", {"start": v(-75.2, -55.42) * mm, "end": v(-69.2, -55.42) * mm, "construction": true});
            skSolve(sketch);
        }
        {
            var Q0;
            Q0 = qSketchRegion(id + "F14", true);
            extrude(context, id + "F15", {"entities" : qUnion([Q0]), "operationType" : NewBodyOperationType.REMOVE, "oppositeDirection" : true, "depth" : 0.5 * mm});
        }
    });
